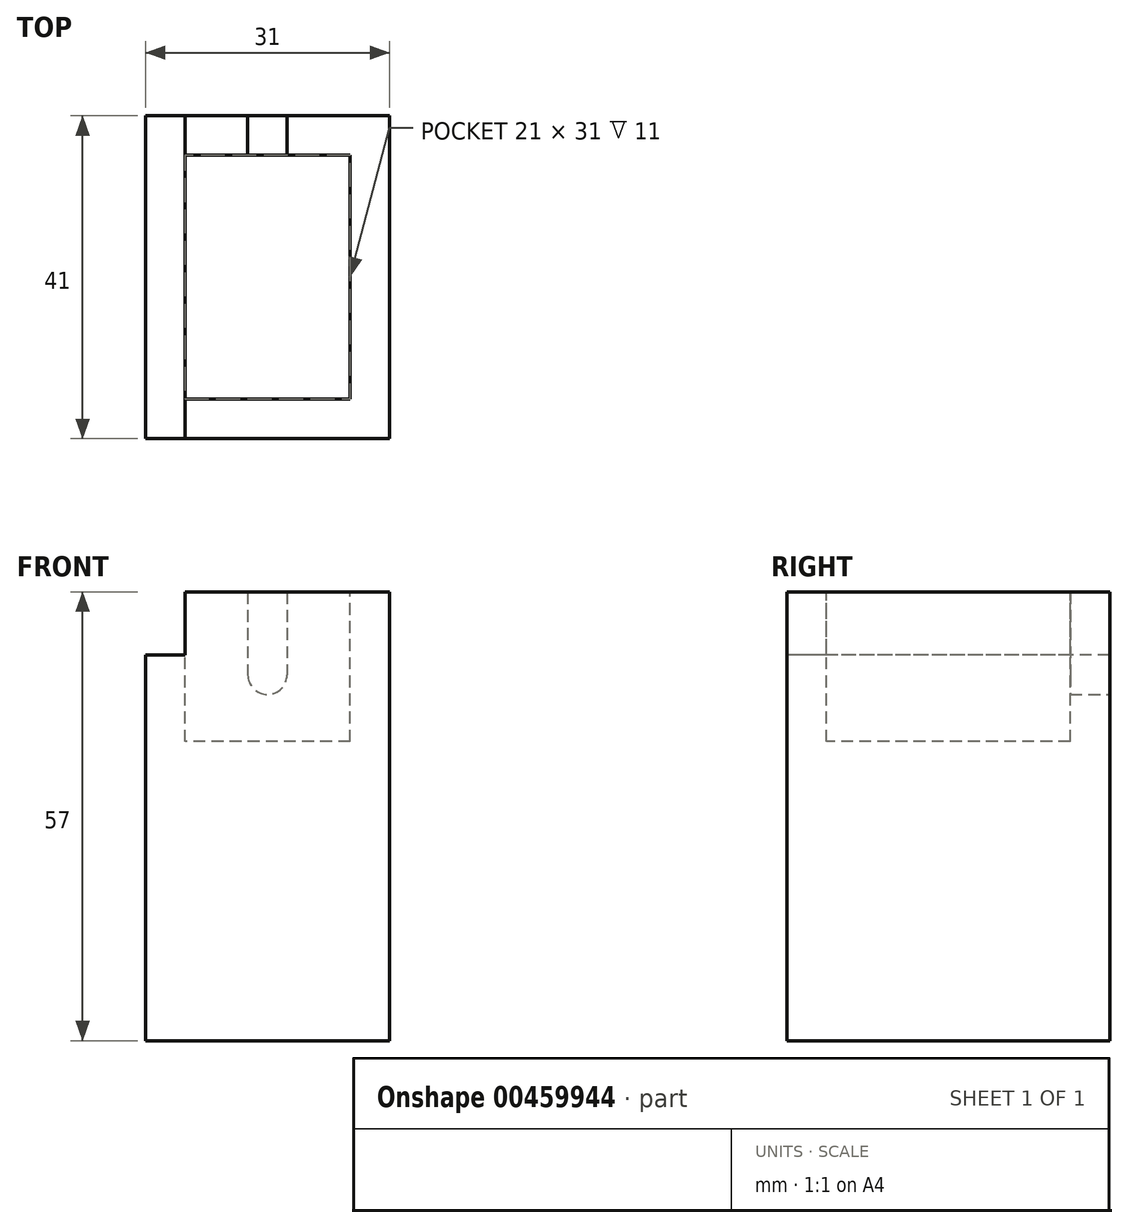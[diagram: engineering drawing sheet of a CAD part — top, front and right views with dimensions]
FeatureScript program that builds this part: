
annotation { "Feature Type Name" : "Feature", "Feature Type Description" : "" }
export const myFeature = defineFeature(function(context is Context, id is Id, definition is map)
    precondition{}
    {
        {
            var Q0;
            Q0=qCreatedBy(makeId("Right.planeOp"),FACE);
            var sketch = newSketch(context, id + "F0", { "sketchPlane" : qUnion([Q0])});
            skLineSegment(sketch, "E0", {"start": v(15.56, 0) * mm, "end": v(-15.44, 0) * mm});
            skLineSegment(sketch, "E1", {"start": v(-15.44, 0) * mm, "end": v(-15.44, 19) * mm});
            skLineSegment(sketch, "E2", {"start": v(15.56, 0) * mm, "end": v(15.56, 19) * mm});
            skLineSegment(sketch, "E3", {"start": v(-15.44, 19) * mm, "end": v(-20.44, 19) * mm});
            skLineSegment(sketch, "E4", {"start": v(-20.44, 19) * mm, "end": v(-20.44, 0) * mm});
            skLineSegment(sketch, "E5", {"start": v(-20.44, 0) * mm, "end": v(-20.44, -38) * mm});
            skLineSegment(sketch, "E6", {"start": v(-20.44, -38) * mm, "end": v(-15.44, -38) * mm});
            skLineSegment(sketch, "E7", {"start": v(-15.44, -38) * mm, "end": v(15.47, -38) * mm});
            skLineSegment(sketch, "E8", {"start": v(15.47, -38) * mm, "end": v(20.56, -38) * mm});
            skLineSegment(sketch, "E9", {"start": v(20.56, -38) * mm, "end": v(20.56, -38) * mm});
            skLineSegment(sketch, "E10", {"start": v(20.56, 0) * mm, "end": v(20.56, 19) * mm});
            skLineSegment(sketch, "E11", {"start": v(15.56, 19) * mm, "end": v(20.56, 19) * mm});
            skLineSegment(sketch, "E12", {"start": v(20.56, 0) * mm, "end": v(20.56, -38) * mm});
            skSolve(sketch);
        }
        {
            var Q0;
            Q0=makeQuery(id+"F0.imprint","IMPRINT",FACE,{"disambiguationData":[TD([[makeQuery(id+"F0.imprint","IMPRINT",EDGE,{"derivedFrom":sQuery(id+"F0.wireOp",EDGE,"E0")}),1.0]])]});
            extrude(context, id + "F1", {"entities" : qUnion([Q0]), "depth" : 21 * mm});
        }
        {
            var Q0;
            Q0=makeQuery(id+"F1.opExtrude","CAP_FACE",FACE,{"disambiguationData":[OSD([sQuery(id+"F0.wireOp",EDGE,"E0"),sQuery(id+"F0.wireOp",EDGE,"E1"),sQuery(id+"F0.wireOp",EDGE,"E2"),sQuery(id+"F0.wireOp",EDGE,"E3"),sQuery(id+"F0.wireOp",EDGE,"E4"),sQuery(id+"F0.wireOp",EDGE,"E5"),sQuery(id+"F0.wireOp",EDGE,"E6"),sQuery(id+"F0.wireOp",EDGE,"E7"),sQuery(id+"F0.wireOp",EDGE,"E8"),sQuery(id+"F0.wireOp",EDGE,"E10"),sQuery(id+"F0.wireOp",EDGE,"E11"),sQuery(id+"F0.wireOp",EDGE,"E12")])],"isStart":false});
            var sketch = newSketch(context, id + "F2", { "sketchPlane" : qUnion([Q0])});
            skLineSegment(sketch, "E13", {"start": v(-20.44, 19) * mm, "end": v(-20.44, -38) * mm});
            skLineSegment(sketch, "E14", {"start": v(-20.44, -38) * mm, "end": v(20.56, -38) * mm});
            skLineSegment(sketch, "E15", {"start": v(20.56, -38) * mm, "end": v(20.56, 19) * mm});
            skLineSegment(sketch, "E16", {"start": v(20.56, 19) * mm, "end": v(-20.44, 19) * mm});
            skSolve(sketch);
        }
        {
            var Q0;
            Q0 = qSketchRegion(id + "F2", true);
            extrude(context, id + "F3", {"entities" : qUnion([Q0]), "operationType" : NewBodyOperationType.ADD, "depth" : 5 * mm});
        }
        {
            var Q0;
            Q0=makeQuery(id+"F1.opExtrude","CAP_FACE",FACE,{"disambiguationData":[OSD([sQuery(id+"F0.wireOp",EDGE,"E0"),sQuery(id+"F0.wireOp",EDGE,"E1"),sQuery(id+"F0.wireOp",EDGE,"E2"),sQuery(id+"F0.wireOp",EDGE,"E3"),sQuery(id+"F0.wireOp",EDGE,"E4"),sQuery(id+"F0.wireOp",EDGE,"E5"),sQuery(id+"F0.wireOp",EDGE,"E6"),sQuery(id+"F0.wireOp",EDGE,"E7"),sQuery(id+"F0.wireOp",EDGE,"E8"),sQuery(id+"F0.wireOp",EDGE,"E10"),sQuery(id+"F0.wireOp",EDGE,"E11"),sQuery(id+"F0.wireOp",EDGE,"E12")])],"isStart":true});
            var sketch = newSketch(context, id + "F4", { "sketchPlane" : qUnion([Q0])});
            skLineSegment(sketch, "E17", {"start": v(-20.56, 11) * mm, "end": v(20.44, 11) * mm});
            skLineSegment(sketch, "E18", {"start": v(20.44, 11) * mm, "end": v(20.44, -38) * mm});
            skLineSegment(sketch, "E19", {"start": v(20.44, -38) * mm, "end": v(-20.56, -38) * mm});
            skLineSegment(sketch, "E20", {"start": v(-20.56, -38) * mm, "end": v(-20.56, 11) * mm});
            skSolve(sketch);
        }
        {
            var Q0;
            Q0 = qSketchRegion(id + "F4", true);
            extrude(context, id + "F5", {"entities" : qUnion([Q0]), "operationType" : NewBodyOperationType.ADD, "depth" : 5 * mm});
        }
        {
            var Q0;
            Q0=makeQuery(id+"F5.boolean.opBoolean","MERGE",FACE,{"derivedFrom":[makeQuery(id+"F3.boolean.opBoolean","MERGE",FACE,{"derivedFrom":[makeQuery(id+"F1.opExtrude","SWEPT_FACE",FACE,{"disambiguationData":[OSD([sQuery(id+"F0.wireOp",EDGE,"E10"),sQuery(id+"F0.wireOp",EDGE,"E12")])]}),makeQuery(id+"F3.opExtrude","SWEPT_FACE",FACE,{"disambiguationData":[OSD([sQuery(id+"F2.wireOp",EDGE,"E15")])]})]}),makeQuery(id+"F5.opExtrude","SWEPT_FACE",FACE,{"disambiguationData":[OSD([sQuery(id+"F4.wireOp",EDGE,"E20")])]})]});
            var sketch = newSketch(context, id + "F6", { "sketchPlane" : qUnion([Q0])});
            skLineSegment(sketch, "E21", {"start": v(-8, 19) * mm, "end": v(-8, 8.49) * mm});
            skLineSegment(sketch, "E22", {"start": v(-13, 19) * mm, "end": v(-13, 8.49) * mm});
            skLineSegment(sketch, "E23", {"start": v(-8, 19) * mm, "end": v(-13, 19) * mm});
            skArc(sketch, "E24", {"start": v(-13, 8.49) * mm, "mid": v(-10.5, 5.99) * mm, "end": v(-8, 8.49) * mm});
            skSolve(sketch);
        }
        {
            var Q0;
            Q0 = qSketchRegion(id + "F6", true);
            extrude(context, id + "F7", {"entities" : qUnion([Q0]), "operationType" : NewBodyOperationType.REMOVE, "oppositeDirection" : true, "depth" : 5 * mm});
        }
    });
